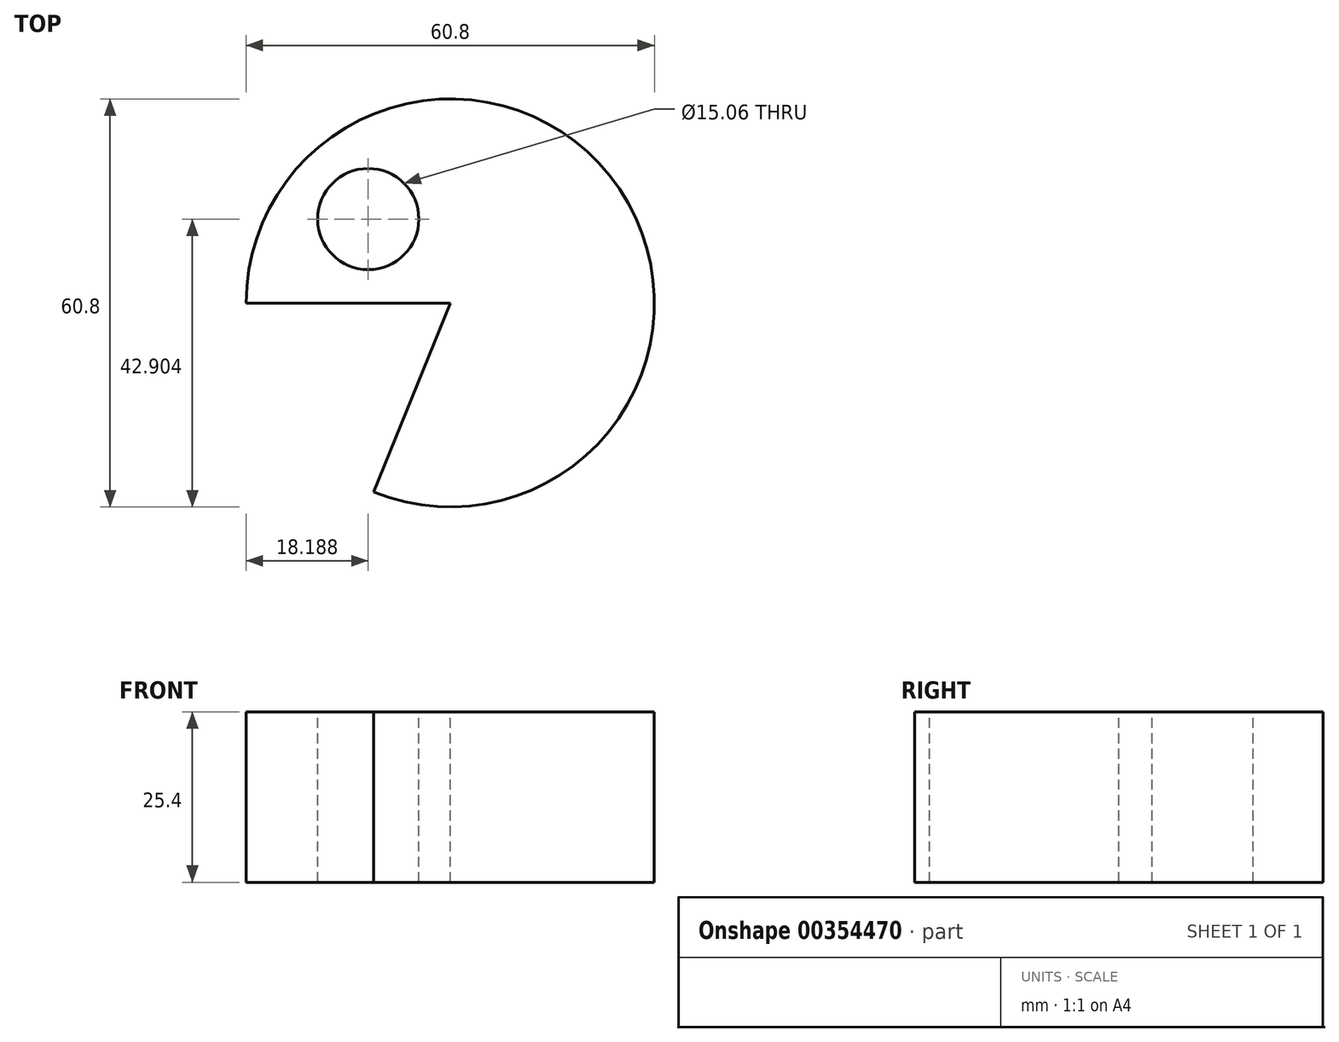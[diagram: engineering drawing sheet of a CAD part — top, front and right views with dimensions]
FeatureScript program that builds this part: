
annotation { "Feature Type Name" : "Feature", "Feature Type Description" : "" }
export const myFeature = defineFeature(function(context is Context, id is Id, definition is map)
    precondition{}
    {
        {
            var Q0;
            Q0=qCreatedBy(makeId("Top.planeOp"),FACE);
            var sketch = newSketch(context, id + "F0", { "sketchPlane" : qUnion([Q0])});
            skCircle(sketch, "E0", {"center": v(0, 0) * mm, "radius": 30.4 * mm});
            skSolve(sketch);
        }
        {
            var Q0;
            Q0 = qSketchRegion(id + "F0", true);
            extrude(context, id + "F1", {"entities" : qUnion([Q0]), "depth" : 25.4 * mm});
        }
        {
            var Q0;
            Q0=makeQuery(id+"F1.opExtrude","CAP_FACE",FACE,{"disambiguationData":[OSD([sQuery(id+"F0.wireOp",EDGE,"E0")])],"isStart":false});
            var sketch = newSketch(context, id + "F2", { "sketchPlane" : qUnion([Q0])});
            skLineSegment(sketch, "E1", {"start": v(-30.4, 0) * mm, "end": v(0, 0) * mm});
            skLineSegment(sketch, "E2", {"start": v(0, 0) * mm, "end": v(-11.42, -28.17) * mm});
            skLineSegment(sketch, "E3", {"start": v(-11.42, -28.17) * mm, "end": v(-30.4, -28.17) * mm});
            skLineSegment(sketch, "E4", {"start": v(-30.4, -28.17) * mm, "end": v(-30.4, 0) * mm});
            skSolve(sketch);
        }
        {
            var Q0;
            Q0 = qSketchRegion(id + "F2", true);
            var Q1;
            Q1 = qSketchRegion(id + "F4", true);
            extrude(context, id + "F3", {"entities" : qUnion([Q0, Q1]), "operationType" : NewBodyOperationType.REMOVE, "oppositeDirection" : true, "depth" : 25.4 * mm});
        }
        {
            var Q0;
            Q0=makeQuery(id+"F1.opExtrude","CAP_FACE",FACE,{"disambiguationData":[OSD([sQuery(id+"F0.wireOp",EDGE,"E0")])],"isStart":false});
            var sketch = newSketch(context, id + "F4", { "sketchPlane" : qUnion([Q0])});
            skPoint(sketch, "E5", {"position": v(25.21, 16.98) * mm});
            skCircle(sketch, "E6", {"center": v(-12.21, 12.5) * mm, "radius": 7.53 * mm});
            skSolve(sketch);
        }
        {
            var Q0;
            Q0 = qSketchRegion(id + "F4", true);
            extrude(context, id + "F5", {"entities" : qUnion([Q0]), "operationType" : NewBodyOperationType.REMOVE, "oppositeDirection" : true, "depth" : 25.4 * mm});
        }
    });
